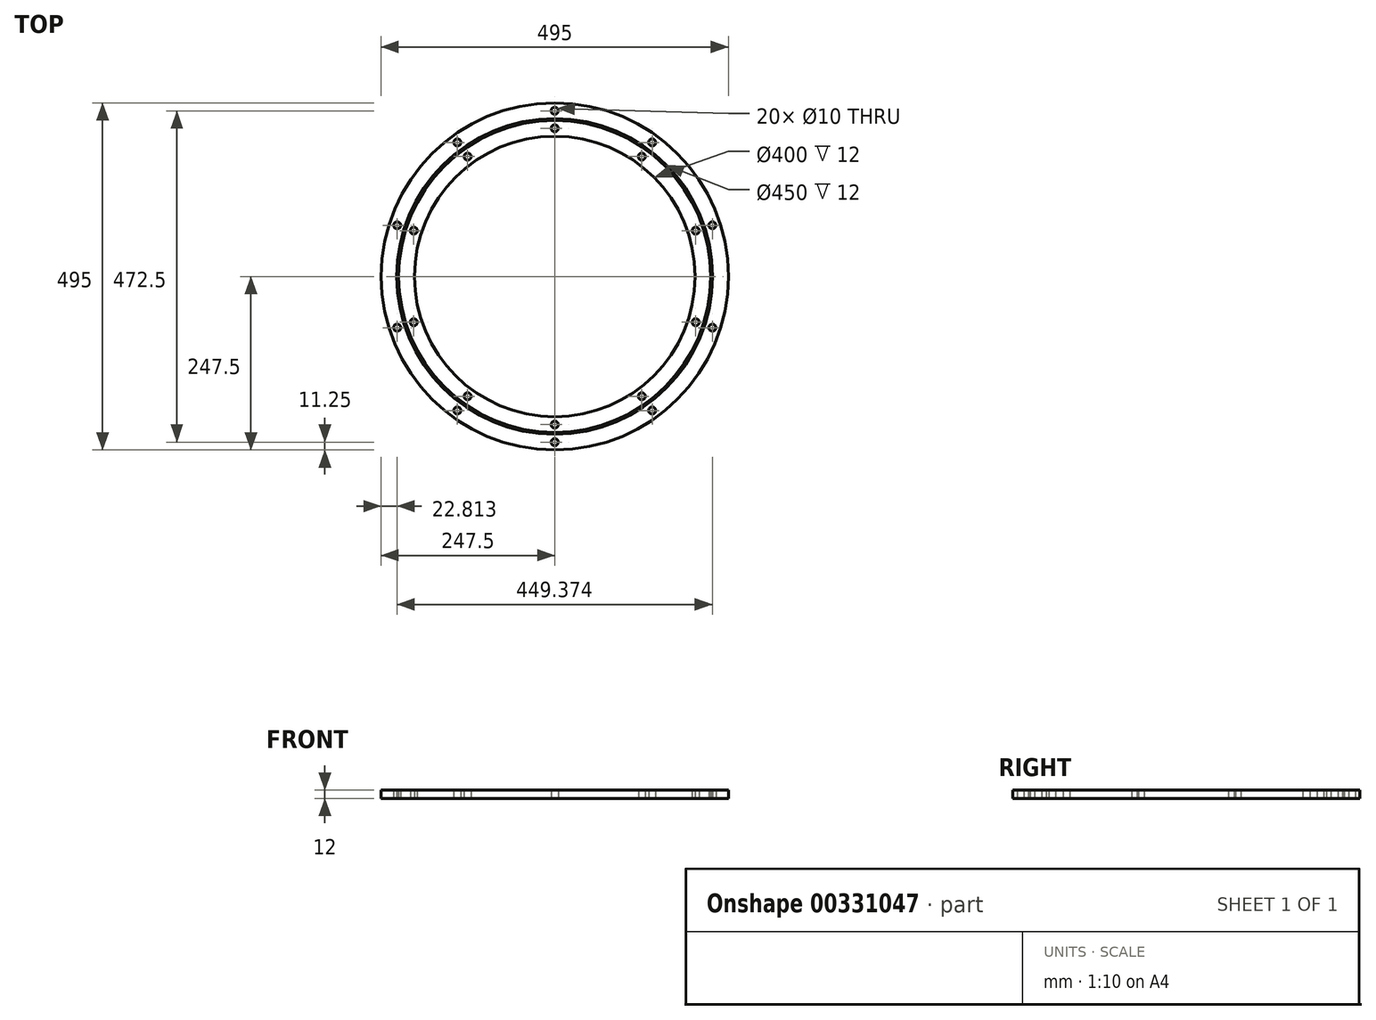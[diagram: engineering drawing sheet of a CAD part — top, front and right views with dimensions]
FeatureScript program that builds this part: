
annotation { "Feature Type Name" : "Feature", "Feature Type Description" : "" }
export const myFeature = defineFeature(function(context is Context, id is Id, definition is map)
    precondition{}
    {
        {
            var Q0;
            Q0=qCreatedBy(makeId("Top.planeOp"),FACE);
            var sketch = newSketch(context, id + "F0", { "sketchPlane" : qUnion([Q0])});
            skCircle(sketch, "E0", {"center": v(0, 0) * mm, "radius": 200 * mm});
            skCircle(sketch, "E1", {"center": v(0, 0) * mm, "radius": 222.5 * mm});
            skCircle(sketch, "E2", {"center": v(0, 0) * mm, "radius": 225 * mm});
            skCircle(sketch, "E3", {"center": v(0, 0) * mm, "radius": 247.5 * mm});
            skLineSegment(sketch, "E4", {"start": v(0, 225) * mm, "end": v(0, 236.25) * mm});
            skLineSegment(sketch, "E5", {"start": v(0, 200) * mm, "end": v(0, 211.25) * mm});
            skLineSegment(sketch, "E6", {"start": v(0, 0) * mm, "end": v(0, 301.4) * mm});
            skCircle(sketch, "E7", {"center": v(0, 236.25) * mm, "radius": 5 * mm});
            skCircle(sketch, "E8", {"center": v(0, 211.25) * mm, "radius": 5 * mm});
            skCircle(sketch, "E9.1.0", {"center": v(138.86, 191.13) * mm, "radius": 5 * mm});
            skCircle(sketch, "E9.1.1", {"center": v(124.17, 170.9) * mm, "radius": 5 * mm});
            skCircle(sketch, "E9.2.0", {"center": v(224.69, 73) * mm, "radius": 5 * mm});
            skCircle(sketch, "E9.2.1", {"center": v(200.91, 65.28) * mm, "radius": 5 * mm});
            skLineSegment(sketch, "E9.anchor1", {"start": v(0, 0) * mm, "end": v(0, 236.25) * mm, "construction": true});
            skLineSegment(sketch, "E9.anchor2", {"start": v(0, 0) * mm, "end": v(224.69, 73) * mm, "construction": true});
            skCircle(sketch, "E10.1.0", {"center": v(224.69, -73) * mm, "radius": 5 * mm});
            skCircle(sketch, "E10.1.1", {"center": v(200.91, -65.28) * mm, "radius": 5 * mm});
            skCircle(sketch, "E10.2.0", {"center": v(138.86, -191.13) * mm, "radius": 5 * mm});
            skCircle(sketch, "E10.2.1", {"center": v(124.17, -170.9) * mm, "radius": 5 * mm});
            skLineSegment(sketch, "E10.anchor2", {"start": v(0, 0) * mm, "end": v(138.86, -191.13) * mm, "construction": true});
            skCircle(sketch, "E11.1.0", {"center": v(0, -211.25) * mm, "radius": 5 * mm});
            skCircle(sketch, "E11.1.1", {"center": v(0, -236.25) * mm, "radius": 5 * mm});
            skCircle(sketch, "E11.2.0", {"center": v(-124.17, -170.9) * mm, "radius": 5 * mm});
            skCircle(sketch, "E11.2.1", {"center": v(-138.86, -191.13) * mm, "radius": 5 * mm});
            skLineSegment(sketch, "E11.anchor1", {"start": v(0, 0) * mm, "end": v(124.17, -170.9) * mm, "construction": true});
            skLineSegment(sketch, "E11.anchor2", {"start": v(0, 0) * mm, "end": v(-124.17, -170.9) * mm, "construction": true});
            skCircle(sketch, "E12.1.0", {"center": v(-200.91, -65.28) * mm, "radius": 5 * mm});
            skCircle(sketch, "E12.1.1", {"center": v(-224.69, -73) * mm, "radius": 5 * mm});
            skCircle(sketch, "E12.2.0", {"center": v(-200.91, 65.28) * mm, "radius": 5 * mm});
            skCircle(sketch, "E12.2.1", {"center": v(-224.69, 73) * mm, "radius": 5 * mm});
            skLineSegment(sketch, "E12.anchor2", {"start": v(0, 0) * mm, "end": v(-200.91, 65.28) * mm, "construction": true});
            skCircle(sketch, "E13.1.0", {"center": v(-138.86, 191.13) * mm, "radius": 5 * mm});
            skCircle(sketch, "E13.1.1", {"center": v(-124.17, 170.9) * mm, "radius": 5 * mm});
            skLineSegment(sketch, "E13.anchor1", {"start": v(0, 0) * mm, "end": v(-224.69, 73) * mm, "construction": true});
            skSolve(sketch);
        }
        {
            var Q0;
            Q0=makeQuery(id+"F0.imprint","IMPRINT",FACE,{"disambiguationData":[TD([[makeQuery(id+"F0.imprint","IMPRINT",EDGE,{"derivedFrom":sQuery(id+"F0.wireOp",EDGE,"E2")}),-1.0]])]});
            var Q1;
            Q1=makeQuery(id+"F0.imprint","IMPRINT",FACE,{"disambiguationData":[TD([[makeQuery(id+"F0.imprint","IMPRINT",EDGE,{"derivedFrom":sQuery(id+"F0.wireOp",EDGE,"E0")}),-1.0]])]});
            extrude(context, id + "F1", {"entities" : qUnion([Q0, Q1]), "depth" : 12 * mm});
        }
    });
